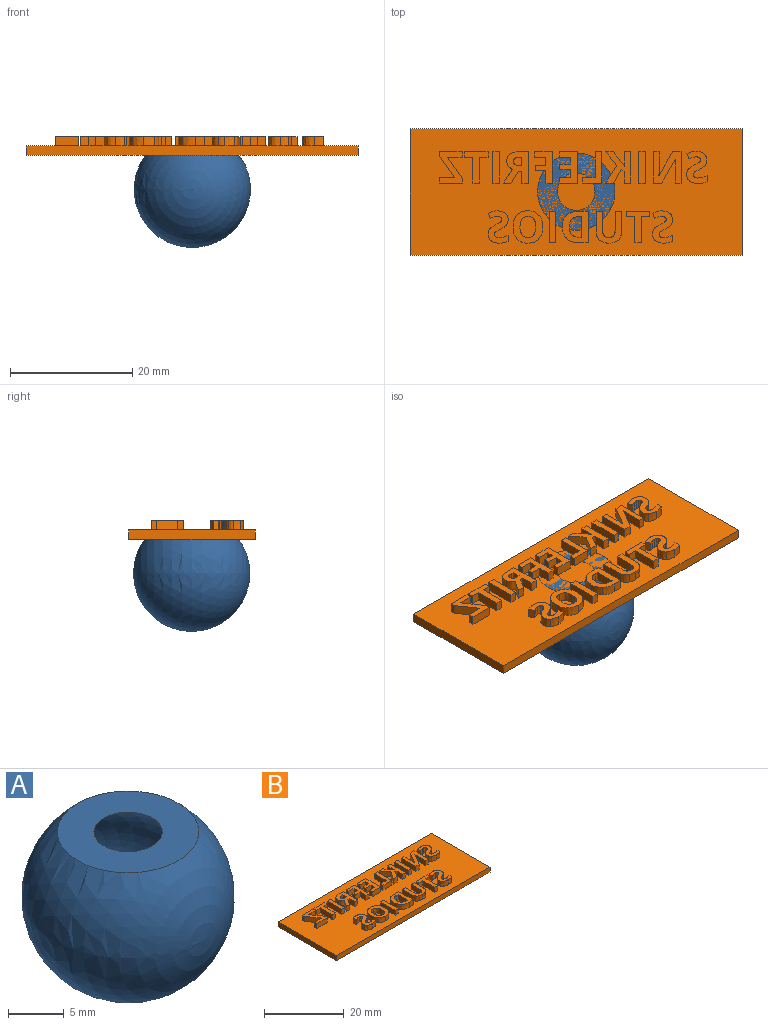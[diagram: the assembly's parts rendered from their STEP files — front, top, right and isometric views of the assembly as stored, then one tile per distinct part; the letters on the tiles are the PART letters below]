
ASSEMBLY  parts=2 mates=1
PART A: 3 faces, bbox 19x19x19 mm
  f0: sphere r=9.52mm, area 995.2mm2, adj f1
  f1: plane 12.66x12.66mm, normal (0,0,1), area 96.4mm2, adj f0,f2
  f2: sphere r=7.74mm, area 722.8mm2, adj f1
PART B: 264 faces, bbox 54.4x20.7x3 mm
  f0: plane 54.35x20.75mm, normal (0,0,1), area 934.2mm2, adj f1,f2,f3,f4,f6,f7,f8,f9
  f1: plane 54.35x1.52mm, normal (0,1,0), area 82.8mm2, adj f0,f2,f4,f5
  f2: plane 20.75x1.52mm, normal (-1,0,0), area 31.6mm2, adj f0,f1,f3,f5
  f3: plane 54.35x1.52mm, normal (0,-1,0), area 82.8mm2, adj f0,f2,f4,f5
  f4: plane 20.75x1.52mm, normal (1,0,0), area 31.6mm2, adj f0,f1,f3,f5
  f5: plane 54.35x20.75mm, normal (0,0,-1), area 1127.7mm2, adj f1,f2,f3,f4
  f6: extruded ~1.52x0.85mm, area 1.4mm2, adj f0,f7,f33,f34
  f7: extruded ~1.52x1.09mm, area 1.9mm2, adj f0,f6,f8,f34
  f8: extruded ~1.52x1.39mm, area 2.2mm2, adj f0,f7,f9,f34
  f9: extruded ~1.52x1.45mm, area 2.3mm2, adj f0,f8,f10,f34
  f10: plane 1.52x1.01mm, normal (1,0,0), area 1.5mm2, adj f0,f9,f11,f34
  f11: extruded ~1.52x0.88mm, area 1.4mm2, adj f0,f10,f12,f34
  f12: extruded ~1.52x0.66mm, area 1mm2, adj f0,f11,f13,f34
  f13: extruded ~1.52x0.55mm, area 0.9mm2, adj f0,f12,f14,f34
  f14: extruded ~1.52x0.41mm, area 0.7mm2, adj f0,f13,f15,f34
  f15: extruded ~1.52x0.27mm, area 0.4mm2, adj f0,f14,f16,f34
  f16: extruded ~1.52x0.25mm, area 0.5mm2, adj f0,f15,f17,f34
  f17: extruded ~1.52x0.66mm, area 1.1mm2, adj f0,f16,f18,f34
  f18: extruded ~1.52x0.7mm, area 1.3mm2, adj f0,f17,f19,f34
  f19: extruded ~1.52x0.47mm, area 0.9mm2, adj f0,f18,f20,f34
  f20: extruded ~1.52x0.63mm, area 1mm2, adj f0,f19,f21,f34
  f21: extruded ~1.52x1.07mm, area 1.8mm2, adj f0,f20,f22,f34
  f22: extruded ~1.52x1.27mm, area 2.1mm2, adj f0,f21,f23,f34
  f23: extruded ~1.52x0.76mm, area 1.2mm2, adj f0,f22,f24,f34
  f24: extruded ~1.52x0.76mm, area 1.2mm2, adj f0,f23,f25,f34
  f25: plane 1.52x0.85mm, normal (-0.92,-0.38,0), area 1.4mm2, adj f0,f24,f26,f34
  f26: extruded ~1.52x0.68mm, area 1.1mm2, adj f0,f25,f27,f34
  f27: extruded ~1.52x0.53mm, area 0.8mm2, adj f0,f26,f28,f34
  f28: extruded ~1.52x0.47mm, area 0.8mm2, adj f0,f27,f29,f34
  f29: extruded ~1.52x0.37mm, area 0.6mm2, adj f0,f28,f30,f34
  f30: extruded ~1.52x0.25mm, area 0.4mm2, adj f0,f29,f31,f34
  f31: extruded ~1.52x0.21mm, area 0.5mm2, adj f0,f30,f32,f34
  f32: extruded ~1.52x0.69mm, area 1.2mm2, adj f0,f31,f33,f34
  f33: extruded ~1.52x0.99mm, area 1.8mm2, adj f0,f6,f32,f34
  f34: plane 5.27x3.34mm, normal (0,0,1), area 9.9mm2, adj f6,f7,f8,f9,f10,f11,f12,f13
  f35: plane 5.12x1.52mm, normal (-1,0,0), area 7.8mm2, adj f0,f36,f48,f49
  f36: plane 1.52x1.38mm, normal (0,-1,0), area 2.1mm2, adj f0,f35,f37,f49
  f37: plane 3.87x2.23mm, normal (0.87,-0.5,0), area 6.8mm2, adj f0,f36,f38,f49
  f38: plane 1.52x0.03mm, normal (0,-1,0), area 0mm2, adj f0,f37,f39,f49
  f39: extruded ~1.52x1.46mm, area 2.2mm2, adj f0,f38,f40,f49
  f40: plane 2.41x1.52mm, normal (-1,0,0), area 3.7mm2, adj f0,f39,f41,f49
  f41: plane 1.52x0.97mm, normal (0,-1,0), area 1.5mm2, adj f0,f40,f42,f49
  f42: plane 5.12x1.52mm, normal (1,0,0), area 7.8mm2, adj f0,f41,f43,f49
  f43: plane 1.52x1.37mm, normal (0,1,0), area 2.1mm2, adj f0,f42,f44,f49
  f44: plane 3.84x2.22mm, normal (-0.87,0.5,0), area 6.8mm2, adj f0,f43,f45,f49
  f45: plane 1.52x0.02mm, normal (0,1,0), area 0mm2, adj f0,f44,f46,f49
  f46: extruded ~1.52x1.41mm, area 2.2mm2, adj f0,f45,f47,f49
  f47: plane 2.43x1.52mm, normal (1,0,0), area 3.7mm2, adj f0,f46,f48,f49
  f48: plane 1.52x0.98mm, normal (0,1,0), area 1.5mm2, adj f0,f35,f47,f49
  f49: plane 5.12x4.54mm, normal (0,0,1), area 14.9mm2, adj f35,f36,f37,f38,f39,f40,f41,f42
  f50: plane 1.52x1.09mm, normal (0,-1,0), area 1.7mm2, adj f0,f51,f53,f54
  f51: plane 5.12x1.52mm, normal (1,0,0), area 7.8mm2, adj f0,f50,f52,f54
  f52: plane 1.52x1.09mm, normal (0,1,0), area 1.7mm2, adj f0,f51,f53,f54
  f53: plane 5.12x1.52mm, normal (-1,0,0), area 7.8mm2, adj f0,f50,f52,f54
  f54: plane 5.12x1.09mm, normal (0,0,1), area 5.6mm2, adj f50,f51,f52,f53
  f55: plane 2.86x1.8mm, normal (-0.85,0.53,0), area 5.1mm2, adj f0,f56,f67,f68
  f56: plane 1.52x1.23mm, normal (0,-1,0), area 1.9mm2, adj f0,f55,f57,f68
  f57: plane 2.16x1.52mm, normal (0.85,-0.53,0), area 3.9mm2, adj f0,f56,f58,f68
  f58: plane 1.52x0.46mm, normal (-0.58,-0.81,0), area 0.9mm2, adj f0,f57,f59,f68
  f59: plane 1.83x1.52mm, normal (-1,0,0), area 2.8mm2, adj f0,f58,f60,f68
  f60: plane 1.52x1.09mm, normal (0,-1,0), area 1.7mm2, adj f0,f59,f61,f68
  f61: plane 5.12x1.52mm, normal (1,0,0), area 7.8mm2, adj f0,f60,f62,f68
  f62: plane 1.52x1.09mm, normal (0,1,0), area 1.7mm2, adj f0,f61,f63,f68
  f63: plane 2.34x1.52mm, normal (-1,0,0), area 3.6mm2, adj f0,f62,f64,f68
  f64: plane 1.52x0.6mm, normal (0.82,0.58,0), area 1.1mm2, adj f0,f63,f65,f68
  f65: plane 1.74x1.52mm, normal (0.78,0.62,0), area 3.4mm2, adj f0,f64,f66,f68
  f66: plane 1.52x1.21mm, normal (0,1,0), area 1.8mm2, adj f0,f65,f67,f68
  f67: plane 2.27x1.79mm, normal (-0.79,-0.62,0), area 4.4mm2, adj f0,f55,f66,f68
  f68: plane 5.12x4.12mm, normal (0,0,1), area 12mm2, adj f55,f56,f57,f58,f59,f60,f61,f62
  f69: plane 3.16x1.52mm, normal (0,-1,0), area 4.8mm2, adj f0,f70,f74,f75
  f70: plane 5.12x1.52mm, normal (1,0,0), area 7.8mm2, adj f0,f69,f71,f75
  f71: plane 1.52x1.09mm, normal (0,1,0), area 1.7mm2, adj f0,f70,f72,f75
  f72: plane 4.23x1.52mm, normal (-1,0,0), area 6.4mm2, adj f0,f71,f73,f75
  f73: plane 2.08x1.52mm, normal (0,1,0), area 3.2mm2, adj f0,f72,f74,f75
  f74: plane 1.52x0.9mm, normal (-1,0,0), area 1.4mm2, adj f0,f69,f73,f75
  f75: plane 5.12x3.16mm, normal (0,0,1), area 7.4mm2, adj f69,f70,f71,f72,f73,f74
  f76: plane 1.52x0.9mm, normal (-1,0,0), area 1.4mm2, adj f0,f77,f87,f88
  f77: plane 2.95x1.52mm, normal (0,-1,0), area 4.5mm2, adj f0,f76,f78,f88
  f78: plane 5.12x1.52mm, normal (1,0,0), area 7.8mm2, adj f0,f77,f79,f88
  f79: plane 2.95x1.52mm, normal (0,1,0), area 4.5mm2, adj f0,f78,f80,f88
  f80: plane 1.52x0.89mm, normal (-1,0,0), area 1.4mm2, adj f0,f79,f81,f88
  f81: plane 1.86x1.52mm, normal (0,-1,0), area 2.8mm2, adj f0,f80,f82,f88
  f82: plane 1.52x1.12mm, normal (-1,0,0), area 1.7mm2, adj f0,f81,f83,f88
  f83: plane 1.73x1.52mm, normal (0,1,0), area 2.6mm2, adj f0,f82,f84,f88
  f84: plane 1.52x0.89mm, normal (-1,0,0), area 1.4mm2, adj f0,f83,f85,f88
  f85: plane 1.73x1.52mm, normal (0,-1,0), area 2.6mm2, adj f0,f84,f86,f88
  f86: plane 1.52x1.32mm, normal (-1,0,0), area 2mm2, adj f0,f85,f87,f88
  f87: plane 1.86x1.52mm, normal (0,1,0), area 2.8mm2, adj f0,f76,f86,f88
  f88: plane 5.12x2.95mm, normal (0,0,1), area 10.4mm2, adj f76,f77,f78,f79,f80,f81,f82,f83
  f89: plane 2.02x1.52mm, normal (-1,0,0), area 3.1mm2, adj f0,f90,f98,f99
  f90: plane 1.52x1.07mm, normal (0,-1,0), area 1.6mm2, adj f0,f89,f91,f99
  f91: plane 5.12x1.52mm, normal (1,0,0), area 7.8mm2, adj f0,f90,f92,f99
  f92: plane 2.94x1.52mm, normal (0,1,0), area 4.5mm2, adj f0,f91,f93,f99
  f93: plane 1.52x0.89mm, normal (-1,0,0), area 1.4mm2, adj f0,f92,f94,f99
  f94: plane 1.87x1.52mm, normal (0,-1,0), area 2.8mm2, adj f0,f93,f95,f99
  f95: plane 1.52x1.32mm, normal (-1,0,0), area 2mm2, adj f0,f94,f96,f99
  f96: plane 1.74x1.52mm, normal (0,1,0), area 2.6mm2, adj f0,f95,f97,f99
  f97: plane 1.52x0.89mm, normal (-1,0,0), area 1.4mm2, adj f0,f96,f98,f99
  f98: plane 1.74x1.52mm, normal (0,-1,0), area 2.6mm2, adj f0,f89,f97,f99
  f99: plane 5.12x2.94mm, normal (0,0,1), area 8.7mm2, adj f89,f90,f91,f92,f93,f94,f95,f96
  f100: plane 1.52x1.38mm, normal (-1,0,0), area 2.1mm2, adj f101,f118,f119,f120
  f101: plane 1.52x0.35mm, normal (0,1,0), area 0.5mm2, adj f100,f102,f119,f120
  f102: extruded ~1.52x0.76mm, area 1.2mm2, adj f101,f103,f119,f120
  f103: extruded ~1.52x0.54mm, area 0.9mm2, adj f102,f104,f119,f120
  f104: extruded ~1.52x0.52mm, area 0.9mm2, adj f103,f105,f119,f120
  f105: extruded ~1.52x0.78mm, area 1.2mm2, adj f104,f118,f119,f120
  f106: plane 1.52x0.58mm, normal (0,-1,0), area 0.9mm2, adj f0,f107,f117,f119
  f107: plane 1.97x1.52mm, normal (-1,0,0), area 3mm2, adj f0,f106,f108,f119
  f108: plane 1.52x1.09mm, normal (0,-1,0), area 1.7mm2, adj f0,f107,f109,f119
  f109: plane 5.12x1.52mm, normal (1,0,0), area 7.8mm2, adj f0,f108,f110,f119
  f110: plane 1.52x1.49mm, normal (0,1,0), area 2.3mm2, adj f0,f109,f111,f119
  f111: extruded ~1.55x1.52mm, area 2.5mm2, adj f0,f110,f112,f119
  f112: extruded ~1.52x1.15mm, area 2mm2, adj f0,f111,f113,f119
  f113: extruded ~1.52x0.8mm, area 1.3mm2, adj f0,f112,f114,f119
  f114: extruded ~1.52x0.7mm, area 1.4mm2, adj f0,f113,f115,f119
  f115: extruded ~2.23x1.52mm, area 4.1mm2, adj f0,f114,f116,f119
  f116: plane 1.52x1.21mm, normal (0,-1,0), area 1.8mm2, adj f0,f115,f117,f119
  f117: plane 1.97x1.52mm, normal (0.85,-0.53,0), area 3.5mm2, adj f0,f106,f116,f119
  f118: plane 1.52x0.33mm, normal (0,-1,0), area 0.5mm2, adj f100,f105,f119,f120
  f119: plane 5.12x4.09mm, normal (0,0,1), area 12.8mm2, adj f100,f101,f102,f103,f104,f105,f106,f107
  f120: plane 1.38x1.36mm, normal (0,0,1), area 1.7mm2, adj f100,f101,f102,f103,f104,f105,f118
  f121: plane 1.52x1.09mm, normal (0,-1,0), area 1.7mm2, adj f0,f122,f124,f125
  f122: plane 5.12x1.52mm, normal (1,0,0), area 7.8mm2, adj f0,f121,f123,f125
  f123: plane 1.52x1.09mm, normal (0,1,0), area 1.7mm2, adj f0,f122,f124,f125
  f124: plane 5.12x1.52mm, normal (-1,0,0), area 7.8mm2, adj f0,f121,f123,f125
  f125: plane 5.12x1.09mm, normal (0,0,1), area 5.6mm2, adj f121,f122,f123,f124
  f126: plane 4.22x1.52mm, normal (-1,0,0), area 6.4mm2, adj f0,f127,f133,f134
  f127: plane 1.52x1.09mm, normal (0,-1,0), area 1.7mm2, adj f0,f126,f128,f134
  f128: plane 4.22x1.52mm, normal (1,0,0), area 6.4mm2, adj f0,f127,f129,f134
  f129: plane 1.52x1.39mm, normal (0,-1,0), area 2.1mm2, adj f0,f128,f130,f134
  f130: plane 1.52x0.9mm, normal (1,0,0), area 1.4mm2, adj f0,f129,f131,f134
  f131: plane 3.87x1.52mm, normal (0,1,0), area 5.9mm2, adj f0,f130,f132,f134
  f132: plane 1.52x0.9mm, normal (-1,0,0), area 1.4mm2, adj f0,f131,f133,f134
  f133: plane 1.52x1.39mm, normal (0,-1,0), area 2.1mm2, adj f0,f126,f132,f134
  f134: plane 5.12x3.87mm, normal (0,0,1), area 8.1mm2, adj f126,f127,f128,f129,f130,f131,f132,f133
  f135: plane 1.52x0.9mm, normal (-1,0,0), area 1.4mm2, adj f0,f136,f144,f145
  f136: plane 3.81x1.52mm, normal (0,-1,0), area 5.8mm2, adj f0,f135,f137,f145
  f137: plane 1.52x0.7mm, normal (1,0,0), area 1.1mm2, adj f0,f136,f138,f145
  f138: plane 3.52x2.46mm, normal (0.82,0.57,0), area 6.5mm2, adj f0,f137,f139,f145
  f139: plane 2.39x1.52mm, normal (0,-1,0), area 3.6mm2, adj f0,f138,f140,f145
  f140: plane 1.52x0.9mm, normal (1,0,0), area 1.4mm2, adj f0,f139,f141,f145
  f141: plane 3.68x1.52mm, normal (0,1,0), area 5.6mm2, adj f0,f140,f142,f145
  f142: plane 1.52x0.7mm, normal (-1,0,0), area 1.1mm2, adj f0,f141,f143,f145
  f143: plane 3.52x2.45mm, normal (-0.82,-0.57,0), area 6.5mm2, adj f0,f142,f144,f145
  f144: plane 2.52x1.52mm, normal (0,1,0), area 3.8mm2, adj f0,f135,f143,f145
  f145: plane 5.12x3.81mm, normal (0,0,1), area 10.5mm2, adj f135,f136,f137,f138,f139,f140,f141,f142
  f146: extruded ~1.52x0.85mm, area 1.4mm2, adj f0,f147,f173,f174
  f147: extruded ~1.52x1.09mm, area 1.9mm2, adj f0,f146,f148,f174
  f148: extruded ~1.52x1.39mm, area 2.2mm2, adj f0,f147,f149,f174
  f149: extruded ~1.52x1.45mm, area 2.3mm2, adj f0,f148,f150,f174
  f150: plane 1.52x1.01mm, normal (1,0,0), area 1.5mm2, adj f0,f149,f151,f174
  f151: extruded ~1.52x0.88mm, area 1.4mm2, adj f0,f150,f152,f174
  f152: extruded ~1.52x0.66mm, area 1mm2, adj f0,f151,f153,f174
  f153: extruded ~1.52x0.55mm, area 0.9mm2, adj f0,f152,f154,f174
  f154: extruded ~1.52x0.41mm, area 0.7mm2, adj f0,f153,f155,f174
  f155: extruded ~1.52x0.27mm, area 0.4mm2, adj f0,f154,f156,f174
  f156: extruded ~1.52x0.25mm, area 0.5mm2, adj f0,f155,f157,f174
  f157: extruded ~1.52x0.66mm, area 1.1mm2, adj f0,f156,f158,f174
  f158: extruded ~1.52x0.7mm, area 1.3mm2, adj f0,f157,f159,f174
  f159: extruded ~1.52x0.47mm, area 0.9mm2, adj f0,f158,f160,f174
  f160: extruded ~1.52x0.63mm, area 1mm2, adj f0,f159,f161,f174
  f161: extruded ~1.52x1.07mm, area 1.8mm2, adj f0,f160,f162,f174
  f162: extruded ~1.52x1.27mm, area 2.1mm2, adj f0,f161,f163,f174
  f163: extruded ~1.52x0.76mm, area 1.2mm2, adj f0,f162,f164,f174
  f164: extruded ~1.52x0.76mm, area 1.2mm2, adj f0,f163,f165,f174
  f165: plane 1.52x0.85mm, normal (-0.92,-0.38,0), area 1.4mm2, adj f0,f164,f166,f174
  f166: extruded ~1.52x0.68mm, area 1.1mm2, adj f0,f165,f167,f174
  f167: extruded ~1.52x0.53mm, area 0.8mm2, adj f0,f166,f168,f174
  f168: extruded ~1.52x0.47mm, area 0.8mm2, adj f0,f167,f169,f174
  f169: extruded ~1.52x0.37mm, area 0.6mm2, adj f0,f168,f170,f174
  f170: extruded ~1.52x0.25mm, area 0.4mm2, adj f0,f169,f171,f174
  f171: extruded ~1.52x0.21mm, area 0.5mm2, adj f0,f170,f172,f174
  f172: extruded ~1.52x0.69mm, area 1.2mm2, adj f0,f171,f173,f174
  f173: extruded ~1.52x0.99mm, area 1.8mm2, adj f0,f146,f172,f174
  f174: plane 5.27x3.34mm, normal (0,0,1), area 9.9mm2, adj f146,f147,f148,f149,f150,f151,f152,f153
  f175: plane 4.22x1.52mm, normal (-1,0,0), area 6.4mm2, adj f0,f176,f182,f183
  f176: plane 1.52x1.09mm, normal (0,-1,0), area 1.7mm2, adj f0,f175,f177,f183
  f177: plane 4.22x1.52mm, normal (1,0,0), area 6.4mm2, adj f0,f176,f178,f183
  f178: plane 1.52x1.39mm, normal (0,-1,0), area 2.1mm2, adj f0,f177,f179,f183
  f179: plane 1.52x0.9mm, normal (1,0,0), area 1.4mm2, adj f0,f178,f180,f183
  f180: plane 3.87x1.52mm, normal (0,1,0), area 5.9mm2, adj f0,f179,f181,f183
  f181: plane 1.52x0.9mm, normal (-1,0,0), area 1.4mm2, adj f0,f180,f182,f183
  f182: plane 1.52x1.39mm, normal (0,-1,0), area 2.1mm2, adj f0,f175,f181,f183
  f183: plane 5.12x3.87mm, normal (0,0,1), area 8.1mm2, adj f175,f176,f177,f178,f179,f180,f181,f182
  f184: plane 1.52x1.08mm, normal (0,1,0), area 1.7mm2, adj f0,f185,f198,f199
  f185: plane 3.31x1.52mm, normal (-1,0,0), area 5.1mm2, adj f0,f184,f186,f199
  f186: extruded ~1.52x1mm, area 1.6mm2, adj f0,f185,f187,f199
  f187: extruded ~1.52x0.73mm, area 1.5mm2, adj f0,f186,f188,f199
  f188: extruded ~1.52x1.14mm, area 1.8mm2, adj f0,f187,f189,f199
  f189: extruded ~1.53x1.52mm, area 2.5mm2, adj f0,f188,f190,f199
  f190: extruded ~1.52x1.39mm, area 2.3mm2, adj f0,f189,f191,f199
  f191: plane 3.3x1.52mm, normal (1,0,0), area 5mm2, adj f0,f190,f192,f199
  f192: plane 1.52x1.08mm, normal (0,1,0), area 1.6mm2, adj f0,f191,f193,f199
  f193: plane 3.14x1.52mm, normal (-1,0,0), area 4.8mm2, adj f0,f192,f194,f199
  f194: extruded ~1.52x0.87mm, area 1.4mm2, adj f0,f193,f195,f199
  f195: extruded ~1.52x0.79mm, area 1.3mm2, adj f0,f194,f196,f199
  f196: extruded ~1.52x0.77mm, area 1.3mm2, adj f0,f195,f197,f199
  f197: extruded ~1.52x0.87mm, area 1.4mm2, adj f0,f196,f198,f199
  f198: plane 3.13x1.52mm, normal (1,0,0), area 4.8mm2, adj f0,f184,f197,f199
  f199: plane 5.19x4.2mm, normal (0,0,1), area 12mm2, adj f184,f185,f186,f187,f188,f189,f190,f191
  f200: extruded ~1.85x1.52mm, area 3.1mm2, adj f0,f201,f211,f212
  f201: extruded ~1.94x1.52mm, area 3.2mm2, adj f0,f200,f202,f212
  f202: extruded ~2.08x1.52mm, area 3.4mm2, adj f0,f201,f203,f212
  f203: plane 1.52x1.45mm, normal (0,-1,0), area 2.2mm2, adj f0,f202,f204,f212
  f204: plane 5.12x1.52mm, normal (1,0,0), area 7.8mm2, adj f0,f203,f205,f212
  f205: plane 1.61x1.52mm, normal (0,1,0), area 2.4mm2, adj f0,f204,f211,f212
  f206: extruded ~1.69x1.57mm, area 4mm2, adj f207,f210,f212,f213
  f207: extruded ~1.65x1.52mm, area 3.8mm2, adj f206,f208,f212,f213
  f208: plane 1.52x0.58mm, normal (0,-1,0), area 0.9mm2, adj f207,f209,f212,f213
  f209: plane 3.34x1.52mm, normal (-1,0,0), area 5.1mm2, adj f208,f210,f212,f213
  f210: plane 1.52x0.47mm, normal (0,1,0), area 0.7mm2, adj f206,f209,f212,f213
  f211: extruded ~1.95x1.52mm, area 3.2mm2, adj f0,f200,f205,f212
  f212: plane 5.12x4.25mm, normal (0,0,1), area 13.4mm2, adj f200,f201,f202,f203,f204,f205,f206,f207
  f213: plane 3.34x2.03mm, normal (0,0,1), area 5.9mm2, adj f206,f207,f208,f209,f210
  f214: plane 1.52x1.09mm, normal (0,-1,0), area 1.7mm2, adj f0,f215,f217,f218
  f215: plane 5.12x1.52mm, normal (1,0,0), area 7.8mm2, adj f0,f214,f216,f218
  f216: plane 1.52x1.09mm, normal (0,1,0), area 1.7mm2, adj f0,f215,f217,f218
  f217: plane 5.12x1.52mm, normal (-1,0,0), area 7.8mm2, adj f0,f214,f216,f218
  f218: plane 5.12x1.09mm, normal (0,0,1), area 5.6mm2, adj f214,f215,f216,f217
  f219: extruded ~1.95x1.52mm, area 3.2mm2, adj f0,f220,f232,f233
  f220: extruded ~1.96x1.52mm, area 3.2mm2, adj f0,f219,f221,f233
  f221: extruded ~1.81x1.52mm, area 3mm2, adj f0,f220,f222,f233
  f222: extruded ~1.81x1.52mm, area 3mm2, adj f0,f221,f223,f233
  f223: extruded ~1.96x1.52mm, area 3.2mm2, adj f0,f222,f224,f233
  f224: extruded ~1.95x1.52mm, area 3.2mm2, adj f0,f223,f225,f233
  f225: extruded ~1.81x1.52mm, area 3mm2, adj f0,f224,f232,f233
  f226: extruded ~1.52x1.29mm, area 2.1mm2, adj f227,f231,f233,f234
  f227: extruded ~1.52x1.29mm, area 2.1mm2, adj f226,f228,f233,f234
  f228: extruded ~1.52x0.97mm, area 1.7mm2, adj f227,f229,f233,f234
  f229: extruded ~1.73x1.52mm, area 3.8mm2, adj f228,f230,f233,f234
  f230: extruded ~1.73x1.52mm, area 3.8mm2, adj f229,f231,f233,f234
  f231: extruded ~1.52x0.98mm, area 1.7mm2, adj f226,f230,f233,f234
  f232: extruded ~1.81x1.52mm, area 3mm2, adj f0,f219,f225,f233
  f233: plane 5.27x4.88mm, normal (0,0,1), area 13.7mm2, adj f219,f220,f221,f222,f223,f224,f225,f226
  f234: plane 3.46x2.6mm, normal (0,0,1), area 7.5mm2, adj f226,f227,f228,f229,f230,f231
  f235: extruded ~1.52x0.85mm, area 1.4mm2, adj f0,f236,f262,f263
  f236: extruded ~1.52x1.09mm, area 1.9mm2, adj f0,f235,f237,f263
  f237: extruded ~1.52x1.39mm, area 2.2mm2, adj f0,f236,f238,f263
  f238: extruded ~1.52x1.45mm, area 2.3mm2, adj f0,f237,f239,f263
  f239: plane 1.52x1.01mm, normal (1,0,0), area 1.5mm2, adj f0,f238,f240,f263
  f240: extruded ~1.52x0.88mm, area 1.4mm2, adj f0,f239,f241,f263
  f241: extruded ~1.52x0.66mm, area 1mm2, adj f0,f240,f242,f263
  f242: extruded ~1.52x0.55mm, area 0.9mm2, adj f0,f241,f243,f263
  f243: extruded ~1.52x0.41mm, area 0.7mm2, adj f0,f242,f244,f263
  f244: extruded ~1.52x0.27mm, area 0.4mm2, adj f0,f243,f245,f263
  f245: extruded ~1.52x0.25mm, area 0.5mm2, adj f0,f244,f246,f263
  f246: extruded ~1.52x0.66mm, area 1.1mm2, adj f0,f245,f247,f263
  f247: extruded ~1.52x0.7mm, area 1.3mm2, adj f0,f246,f248,f263
  f248: extruded ~1.52x0.47mm, area 0.9mm2, adj f0,f247,f249,f263
  f249: extruded ~1.52x0.63mm, area 1mm2, adj f0,f248,f250,f263
  f250: extruded ~1.52x1.07mm, area 1.8mm2, adj f0,f249,f251,f263
  f251: extruded ~1.52x1.27mm, area 2.1mm2, adj f0,f250,f252,f263
  f252: extruded ~1.52x0.76mm, area 1.2mm2, adj f0,f251,f253,f263
  f253: extruded ~1.52x0.76mm, area 1.2mm2, adj f0,f252,f254,f263
  f254: plane 1.52x0.85mm, normal (-0.92,-0.38,0), area 1.4mm2, adj f0,f253,f255,f263
  f255: extruded ~1.52x0.68mm, area 1.1mm2, adj f0,f254,f256,f263
  f256: extruded ~1.52x0.53mm, area 0.8mm2, adj f0,f255,f257,f263
  f257: extruded ~1.52x0.47mm, area 0.8mm2, adj f0,f256,f258,f263
  f258: extruded ~1.52x0.37mm, area 0.6mm2, adj f0,f257,f259,f263
  f259: extruded ~1.52x0.25mm, area 0.4mm2, adj f0,f258,f260,f263
  f260: extruded ~1.52x0.21mm, area 0.5mm2, adj f0,f259,f261,f263
  f261: extruded ~1.52x0.69mm, area 1.2mm2, adj f0,f260,f262,f263
  f262: extruded ~1.52x0.99mm, area 1.8mm2, adj f0,f235,f261,f263
  f263: plane 5.27x3.34mm, normal (0,0,1), area 9.9mm2, adj f235,f236,f237,f238,f239,f240,f241,f242
PLACE A t=(29.92,15.79,-7.77)mm
PLACE B t=(-35.23,4.77,-0.66)mm
MATE fastened A.f1 <-> B.f0  axis (0,0,1) through (29.92,15.79,-0.66)mm
